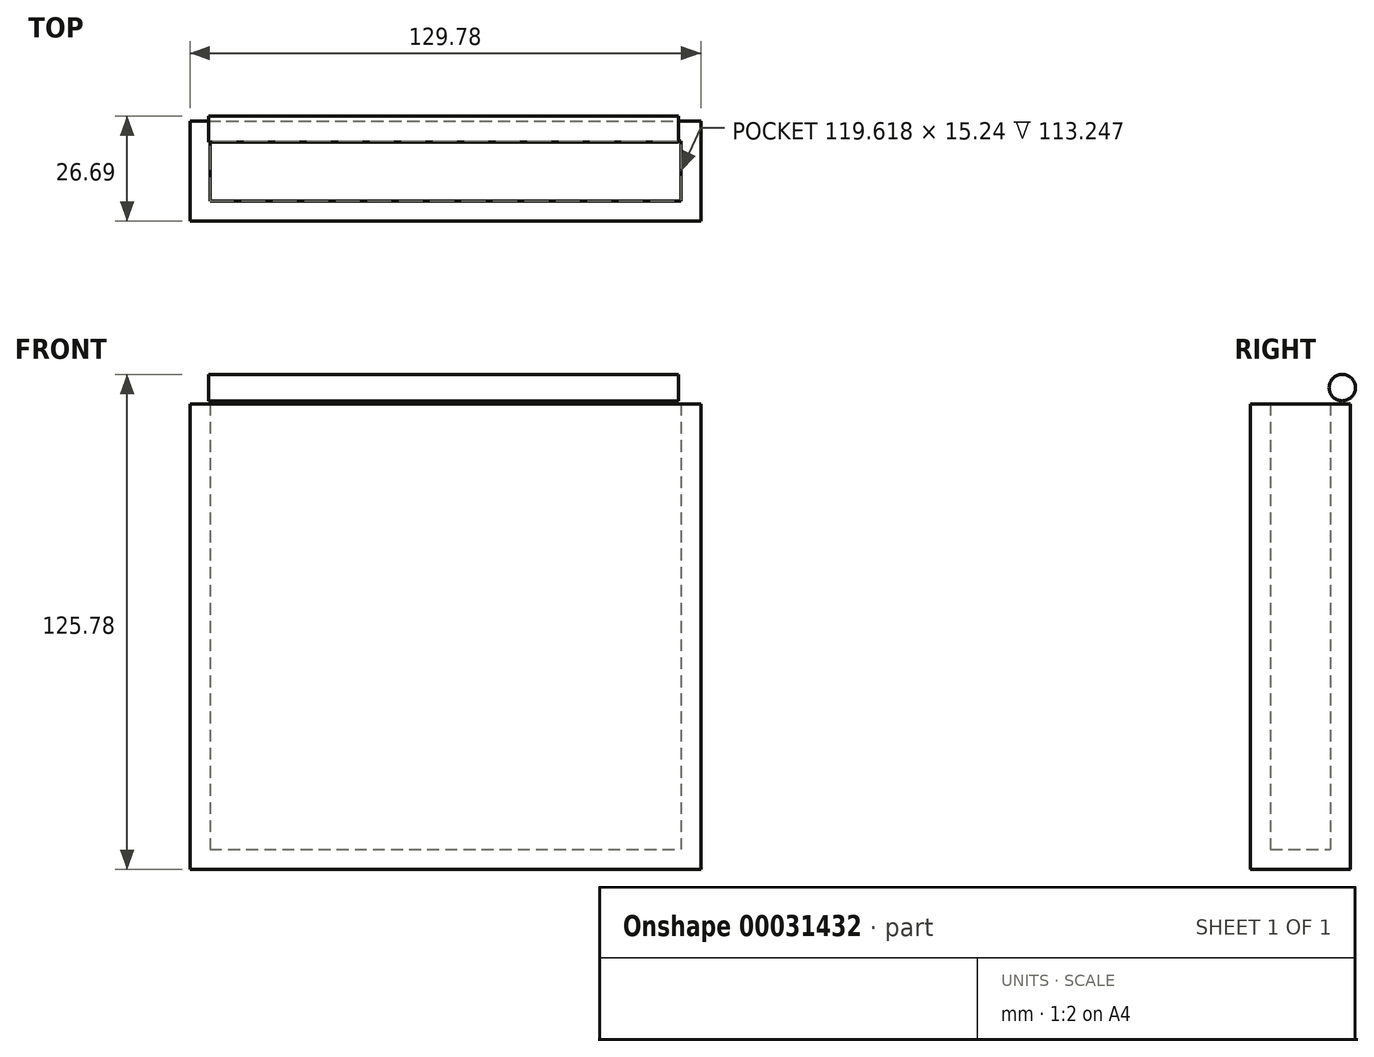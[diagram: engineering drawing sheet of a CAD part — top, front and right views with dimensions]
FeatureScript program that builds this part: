
annotation { "Feature Type Name" : "Feature", "Feature Type Description" : "" }
export const myFeature = defineFeature(function(context is Context, id is Id, definition is map)
    precondition{}
    {
        {
            var Q0;
            Q0=qCreatedBy(makeId("Front.planeOp"),FACE);
            var sketch = newSketch(context, id + "F0", { "sketchPlane" : qUnion([Q0])});
            skLineSegment(sketch, "E0.bottom", {"start": v(-63.13, 60.93) * mm, "end": v(66.65, 60.93) * mm});
            skLineSegment(sketch, "E0.top", {"start": v(-63.13, -57.4) * mm, "end": v(66.65, -57.4) * mm});
            skLineSegment(sketch, "E0.left", {"start": v(-63.13, 60.93) * mm, "end": v(-63.13, -57.4) * mm});
            skLineSegment(sketch, "E0.right", {"start": v(66.65, 60.93) * mm, "end": v(66.65, -57.4) * mm});
            skSolve(sketch);
        }
        {
            var Q0;
            Q0 = qSketchRegion(id + "F0", true);
            extrude(context, id + "F1", {"entities" : qUnion([Q0]), "depth" : 25.4 * mm});
        }
        {
            var Q0;
            Q0=makeQuery(id+"F1.opExtrude","SWEPT_FACE",FACE,{"disambiguationData":[OSD([sQuery(id+"F0.wireOp",EDGE,"E0.bottom")])]});
            shell(context, id + "F2", {"entities" : qUnion([Q0]), "thickness" : 5.08 * mm});
        }
        {
            var Q0;
            Q0=qCreatedBy(makeId("Right.planeOp"),FACE);
            var sketch = newSketch(context, id + "F3", { "sketchPlane" : qUnion([Q0])});
            skCircle(sketch, "E1", {"center": v(-2.06, 65.04) * mm, "radius": 3.35 * mm});
            skPoint(sketch, "E1.first.point", {"position": v(-4.11, 62.4) * mm});
            skPoint(sketch, "E1.second.point", {"position": v(0, 62.4) * mm});
            skPoint(sketch, "E1.third.point", {"position": v(0, 67.68) * mm});
            skSolve(sketch);
        }
        {
            var Q0;
            Q0 = qSketchRegion(id + "F3", true);
            extrude(context, id + "F4", {"entities" : qUnion([Q0]), "depth" : 60.96 * mm, "hasSecondDirection" : true, "secondDirectionOppositeDirection" : true, "secondDirectionDepth" : 58.42 * mm});
        }
    });
